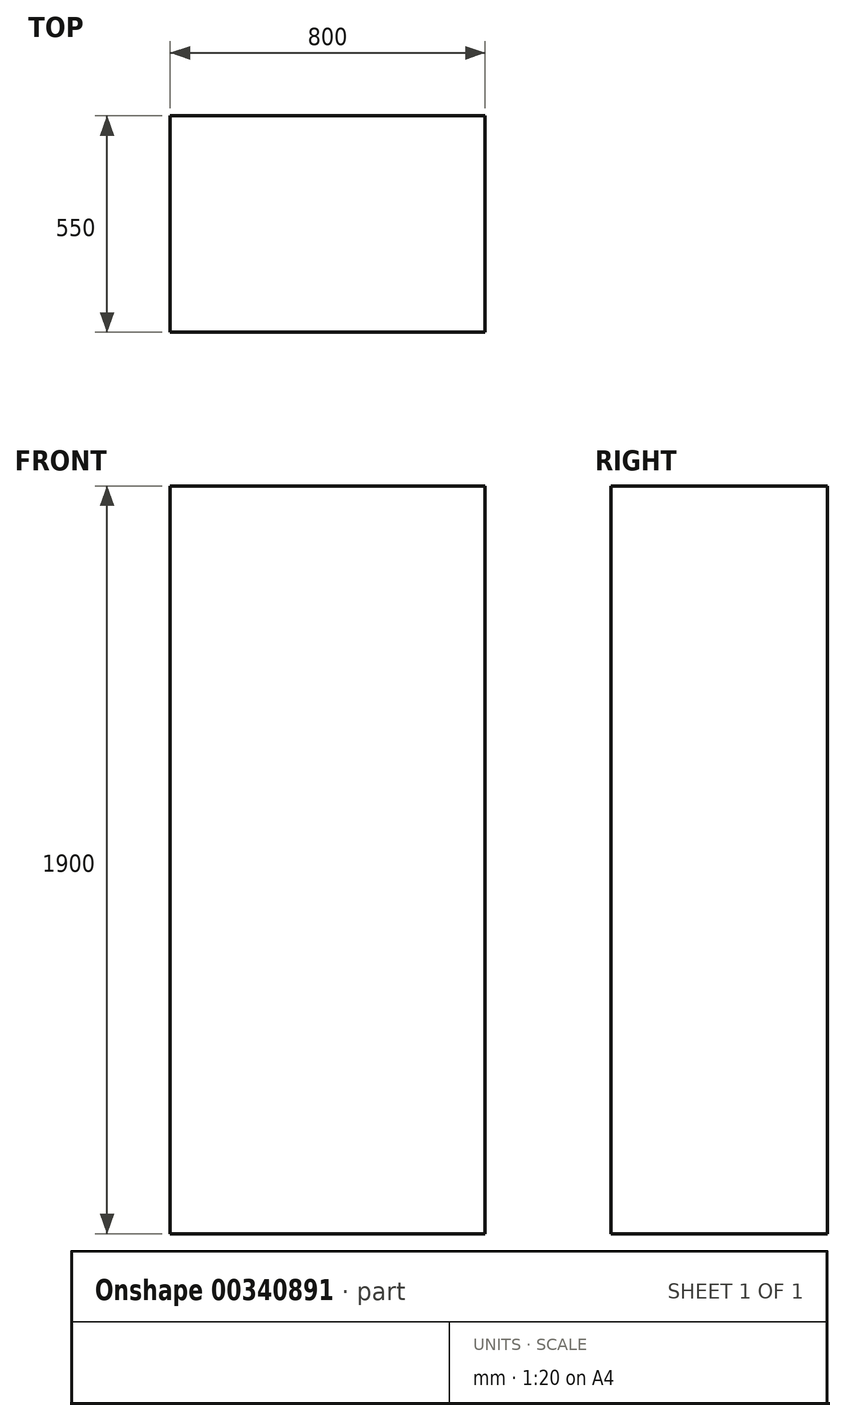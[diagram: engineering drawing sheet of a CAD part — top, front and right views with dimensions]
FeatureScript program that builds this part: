
annotation { "Feature Type Name" : "Feature", "Feature Type Description" : "" }
export const myFeature = defineFeature(function(context is Context, id is Id, definition is map)
    precondition{}
    {
        {
            var Q0;
            Q0=qCreatedBy(makeId("Top.planeOp"),FACE);
            var sketch = newSketch(context, id + "F0", { "sketchPlane" : qUnion([Q0])});
            skLineSegment(sketch, "E0.bottom", {"start": v(-58.82, 507.43) * mm, "end": v(741.18, 507.43) * mm});
            skLineSegment(sketch, "E0.top", {"start": v(-58.82, -42.57) * mm, "end": v(741.18, -42.57) * mm});
            skLineSegment(sketch, "E0.left", {"start": v(-58.82, 507.43) * mm, "end": v(-58.82, -42.57) * mm});
            skLineSegment(sketch, "E0.right", {"start": v(741.18, 507.43) * mm, "end": v(741.18, -42.57) * mm});
            skSolve(sketch);
        }
        {
            var Q0;
            Q0 = qSketchRegion(id + "F0", true);
            extrude(context, id + "F1", {"entities" : qUnion([Q0]), "depth" : 1900 * mm});
        }
    });
